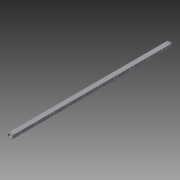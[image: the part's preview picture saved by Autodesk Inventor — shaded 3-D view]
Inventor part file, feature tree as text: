
AUTODESK INVENTOR PART (.ipt)
format: ipt  version: 2015 SP1 (Build 190203100, 203)  size: 189,952 bytes
history: native  units: in
note: dims shown in document units (in); Inventor stores cm internally (conversion verified against a paired STEP export)
features: extrude x3, sketch x1
ambient origin geometry x8: Origin, YZ Plane, XZ Plane, XY Plane, X Axis, Y Axis, Z Axis, Center Point
bodies: Solid1 (feature_tree)
feature tree (4):
  extrude  "Extrusion1"  Depth=1.1811in
  extrude  "Extrusion2"  Depth=0.0787in
  extrude  "Extrusion3"  Depth=56.2992in TaperAngle=0.0deg
  sketch  "Sketch4"  dims[d0=1.5748in d1=1.1811in d3=0.0787in d4=56.2992in d5=0.0in d6=0.0787in d7=0.0787in d8=0.0787in d14=3.937in d16=5.6299in d17=0.3937in d19=0.3937in d21=0.3937in d22=0.0in d23=0.2756in d24=0.4921in d25=0.7087in d26=0.4921in d27=0.0in d28=0.0in]
